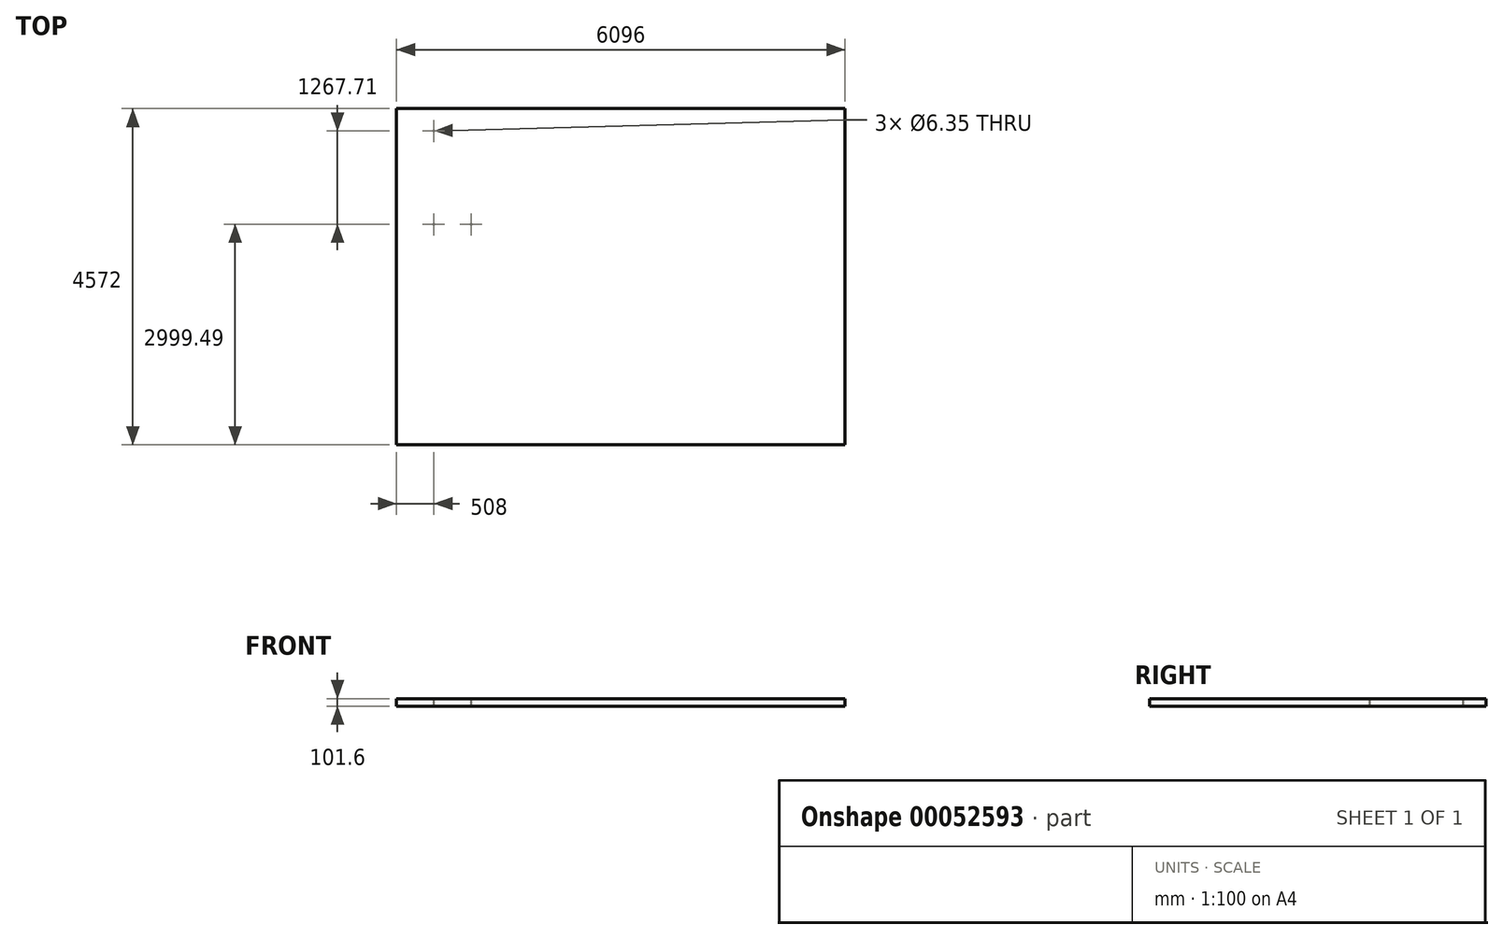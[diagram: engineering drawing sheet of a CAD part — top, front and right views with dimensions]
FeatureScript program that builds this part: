
annotation { "Feature Type Name" : "Feature", "Feature Type Description" : "" }
export const myFeature = defineFeature(function(context is Context, id is Id, definition is map)
    precondition{}
    {
        {
            var Q0;
            Q0=qCreatedBy(makeId("Top.planeOp"),FACE);
            var sketch = newSketch(context, id + "F0", { "sketchPlane" : qUnion([Q0])});
            skLineSegment(sketch, "E0.bottom", {"start": v(0, 0) * mm, "end": v(6096, 0) * mm});
            skLineSegment(sketch, "E0.top", {"start": v(0, 4572) * mm, "end": v(6096, 4572) * mm});
            skLineSegment(sketch, "E0.left", {"start": v(0, 0) * mm, "end": v(0, 4572) * mm});
            skLineSegment(sketch, "E0.right", {"start": v(6096, 0) * mm, "end": v(6096, 4572) * mm});
            skSolve(sketch);
        }
        {
            var Q0;
            Q0=makeQuery(id+"F0.imprint","IMPRINT",FACE,{"disambiguationData":[TD([[makeQuery(id+"F0.imprint","IMPRINT",EDGE,{"derivedFrom":sQuery(id+"F0.wireOp",EDGE,"E0.bottom")}),1.0]])]});
            extrude(context, id + "F1", {"entities" : qUnion([Q0]), "depth" : 101.6 * mm});
        }
        {
            var Q0;
            Q0=makeQuery(id+"F1.opExtrude","CAP_FACE",FACE,{"disambiguationData":[OSD([sQuery(id+"F0.wireOp",EDGE,"E0.bottom"),sQuery(id+"F0.wireOp",EDGE,"E0.top"),sQuery(id+"F0.wireOp",EDGE,"E0.left"),sQuery(id+"F0.wireOp",EDGE,"E0.right")])],"isStart":false});
            var sketch = newSketch(context, id + "F2", { "sketchPlane" : qUnion([Q0])});
            skPoint(sketch, "E1", {"position": v(508, 2999.49) * mm});
            skPoint(sketch, "E2", {"position": v(508, 4267.2) * mm});
            skPoint(sketch, "E3", {"position": v(1016, 2999.49) * mm});
            skPoint(sketch, "E4", {"position": v(1016, 4267.2) * mm});
            skPoint(sketch, "E5", {"position": v(3556, 2999.49) * mm});
            skPoint(sketch, "E6", {"position": v(3556, 4267.2) * mm});
            skSolve(sketch);
        }
        {
            var Q0;
            Q0=sQuery(id+"F2.wireOp",VERTEX,"E1");
            var Q1;
            Q1=sQuery(id+"F2.wireOp",VERTEX,"E3");
            var Q2;
            Q2=sQuery(id+"F2.wireOp",VERTEX,"E2");
            var Q3;
            Q3=makeQuery(id+"F1.opExtrude","SWEPT_BODY",BODY,{"disambiguationData":[OSD([sQuery(id+"F0.wireOp",EDGE,"E0.bottom"),sQuery(id+"F0.wireOp",EDGE,"E0.top"),sQuery(id+"F0.wireOp",EDGE,"E0.left"),sQuery(id+"F0.wireOp",EDGE,"E0.right")])]});
            hole(context, id + "F3", {"style" : HoleStyle.SIMPLE, "holeDiameter" : 6.35 * mm, "endStyle" : HoleEndStyle.THROUGH, "locations" : qUnion([Q0, Q1, Q2]), "scope" : qUnion([Q3])});
        }
    });
